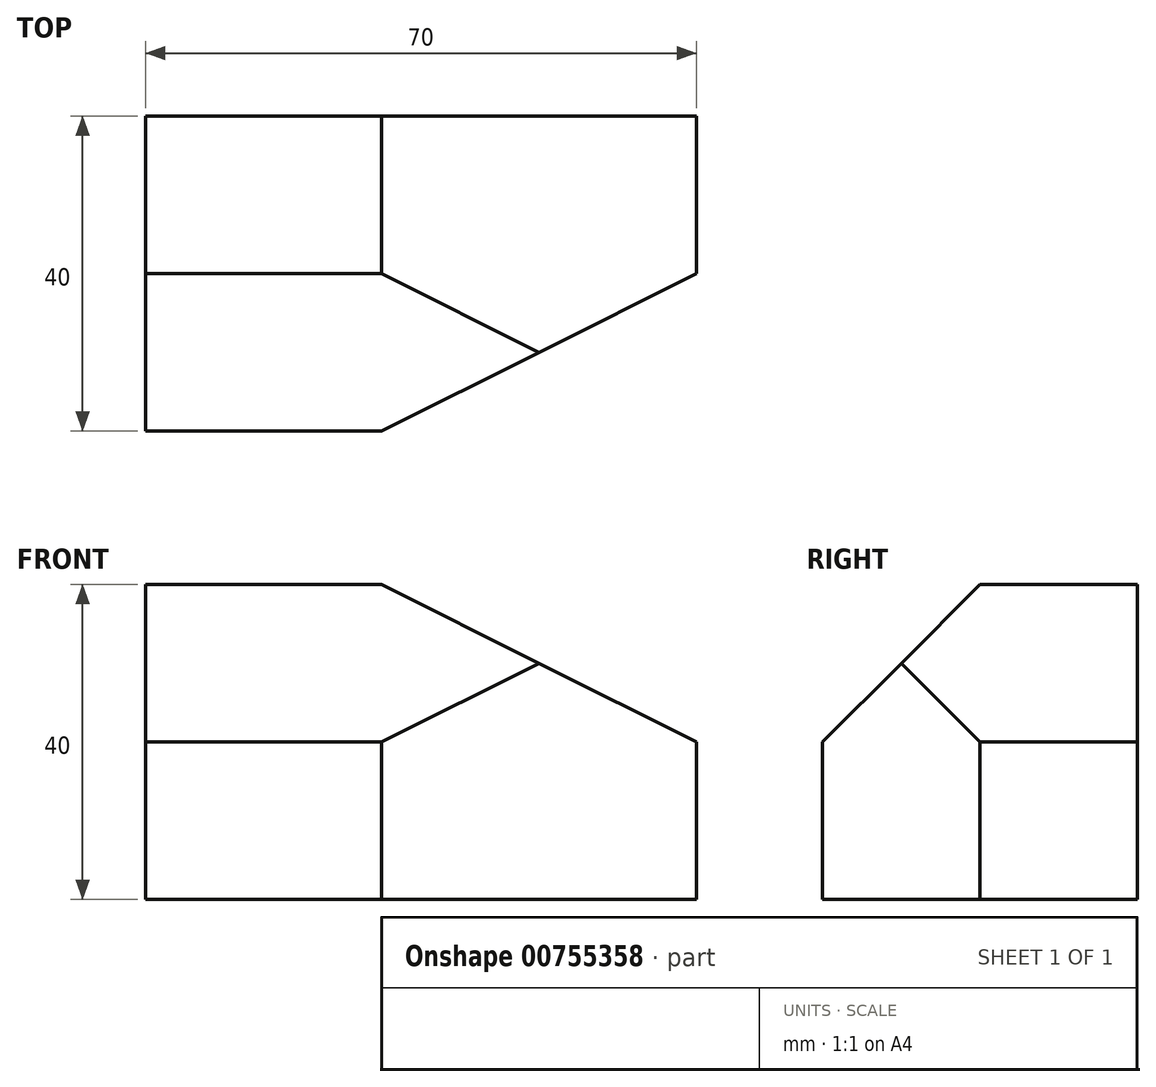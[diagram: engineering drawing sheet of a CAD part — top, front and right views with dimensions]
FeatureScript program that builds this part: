
annotation { "Feature Type Name" : "Feature", "Feature Type Description" : "" }
export const myFeature = defineFeature(function(context is Context, id is Id, definition is map)
    precondition{}
    {
        {
            var Q0;
            Q0=qCreatedBy(makeId("Front.planeOp"),FACE);
            var sketch = newSketch(context, id + "F0", { "sketchPlane" : qUnion([Q0])});
            skLineSegment(sketch, "E0", {"start": v(0, 0) * mm, "end": v(70, 0) * mm});
            skLineSegment(sketch, "E1", {"start": v(70, 0) * mm, "end": v(70, 40) * mm});
            skLineSegment(sketch, "E2", {"start": v(70, 40) * mm, "end": v(0, 40) * mm});
            skLineSegment(sketch, "E3", {"start": v(0, 40) * mm, "end": v(0, 0) * mm});
            skSolve(sketch);
        }
        {
            var Q0;
            Q0=makeQuery(id+"F0.imprint","IMPRINT",FACE,{"disambiguationData":[TD([[makeQuery(id+"F0.imprint","IMPRINT",EDGE,{"derivedFrom":sQuery(id+"F0.wireOp",EDGE,"E0")}),1.0]])]});
            extrude(context, id + "F1", {"entities" : qUnion([Q0]), "depth" : 40 * mm, "offsetDistance" : 25 * mm});
        }
        {
            var Q0;
            Q0=makeQuery(id+"F1.opExtrude","SWEPT_FACE",FACE,{"disambiguationData":[OSD([sQuery(id+"F0.wireOp",EDGE,"E1")])]});
            var sketch = newSketch(context, id + "F2", { "sketchPlane" : qUnion([Q0])});
            skLineSegment(sketch, "E4", {"start": v(-40, 40) * mm, "end": v(-40, 20) * mm});
            skLineSegment(sketch, "E5", {"start": v(-40, 20) * mm, "end": v(-20, 40) * mm});
            skLineSegment(sketch, "E6", {"start": v(-20, 40) * mm, "end": v(-40, 40) * mm});
            skSolve(sketch);
        }
        {
            var Q0;
            Q0=makeQuery(id+"F2.imprint","IMPRINT",FACE,{"disambiguationData":[TD([[makeQuery(id+"F2.imprint","IMPRINT",EDGE,{"derivedFrom":sQuery(id+"F2.wireOp",EDGE,"E4")}),-1.0]])]});
            extrude(context, id + "F3", {"entities" : qUnion([Q0]), "operationType" : NewBodyOperationType.ADD, "depth" : 70 * mm, "offsetDistance" : 25 * mm});
        }
        {
            var Q0;
            Q0=makeQuery(id+"F3.opExtrude","CAP_FACE",FACE,{"disambiguationData":[OSD([sQuery(id+"F2.wireOp",EDGE,"E4"),sQuery(id+"F2.wireOp",EDGE,"E5"),sQuery(id+"F2.wireOp",EDGE,"E6")])],"isStart":false});
            extrude(context, id + "F4", {"entities" : qUnion([Q0]), "operationType" : NewBodyOperationType.REMOVE, "oppositeDirection" : true, "depth" : 140 * mm, "offsetDistance" : 25 * mm});
        }
        {
            var Q0;
            Q0=makeQuery(id+"F1.opExtrude","CAP_FACE",FACE,{"disambiguationData":[OSD([sQuery(id+"F0.wireOp",EDGE,"E0"),sQuery(id+"F0.wireOp",EDGE,"E1"),sQuery(id+"F0.wireOp",EDGE,"E2"),sQuery(id+"F0.wireOp",EDGE,"E3")])],"isStart":true});
            var sketch = newSketch(context, id + "F5", { "sketchPlane" : qUnion([Q0])});
            skLineSegment(sketch, "E7", {"start": v(-70, 20) * mm, "end": v(-30, 20) * mm});
            skLineSegment(sketch, "E8", {"start": v(-30, 20) * mm, "end": v(-30, 40) * mm});
            skLineSegment(sketch, "E9", {"start": v(-30, 40) * mm, "end": v(-70, 20) * mm});
            skSolve(sketch);
        }
        {
            var Q0;
            {var subQ0=sQuery(id+"F5.wireOp",EDGE,"E9");Q0=makeQuery(id+"F5.imprint","IMPRINT",FACE,{"disambiguationData":[TD([[makeQuery(id+"F5.imprint","IMPRINT",EDGE,{"derivedFrom":subQ0}),-1.0]])]});}
            extrude(context, id + "F6", {"entities" : qUnion([Q0]), "operationType" : NewBodyOperationType.REMOVE, "oppositeDirection" : true, "depth" : 40 * mm, "offsetDistance" : 25 * mm});
        }
        {
            var Q0;
            Q0=makeQuery(id+"F1.opExtrude","SWEPT_FACE",FACE,{"disambiguationData":[OSD([sQuery(id+"F0.wireOp",EDGE,"E0")])]});
            var sketch = newSketch(context, id + "F7", { "sketchPlane" : qUnion([Q0])});
            skLineSegment(sketch, "E10", {"start": v(70, 40) * mm, "end": v(30, 40) * mm});
            skLineSegment(sketch, "E11", {"start": v(30, 40) * mm, "end": v(70, 20) * mm});
            skLineSegment(sketch, "E12", {"start": v(70, 20) * mm, "end": v(70, 40) * mm});
            skSolve(sketch);
        }
        {
            var Q0;
            Q0=makeQuery(id+"F7.imprint","IMPRINT",FACE,{"disambiguationData":[TD([[makeQuery(id+"F7.imprint","IMPRINT",EDGE,{"derivedFrom":sQuery(id+"F7.wireOp",EDGE,"E10")}),-1.0]])]});
            extrude(context, id + "F8", {"entities" : qUnion([Q0]), "operationType" : NewBodyOperationType.ADD, "depth" : 40 * mm, "offsetDistance" : 25 * mm});
        }
        {
            var Q0;
            Q0=makeQuery(id+"F8.opExtrude","CAP_FACE",FACE,{"disambiguationData":[OSD([sQuery(id+"F7.wireOp",EDGE,"E10"),sQuery(id+"F7.wireOp",EDGE,"E11"),sQuery(id+"F7.wireOp",EDGE,"E12")])],"isStart":false});
            extrude(context, id + "F9", {"entities" : qUnion([Q0]), "operationType" : NewBodyOperationType.REMOVE, "oppositeDirection" : true, "depth" : 80 * mm, "offsetDistance" : 25 * mm});
        }
        {
            var Q0;
            Q0=makeQuery(id+"F4.boolean.opBoolean","COPY",FACE,{"derivedFrom":makeQuery(id+"F4.opExtrude","SWEPT_FACE",FACE,{"disambiguationData":[OSD([sQuery(id+"F2.wireOp",EDGE,"E5")])]})});
            var sketch = newSketch(context, id + "F10", { "sketchPlane" : qUnion([Q0])});
            skLineSegment(sketch, "E13", {"start": v(30, 14.14) * mm, "end": v(80.6, 0) * mm});
            skLineSegment(sketch, "E14", {"start": v(80.6, 0) * mm, "end": v(30, -14.14) * mm});
            skLineSegment(sketch, "E15", {"start": v(30, -14.14) * mm, "end": v(30, 14.14) * mm});
            skSolve(sketch);
        }
        {
            var Q0;
            Q0=makeQuery(id+"F10.imprint","IMPRINT",FACE,{"disambiguationData":[TD([[makeQuery(id+"F10.imprint","IMPRINT",EDGE,{"derivedFrom":sQuery(id+"F10.wireOp",EDGE,"E15")}),-1.0]])]});
            extrude(context, id + "F11", {"entities" : qUnion([Q0]), "operationType" : NewBodyOperationType.ADD, "oppositeDirection" : true, "depth" : 10 * mm, "offsetDistance" : 25 * mm});
        }
    });
